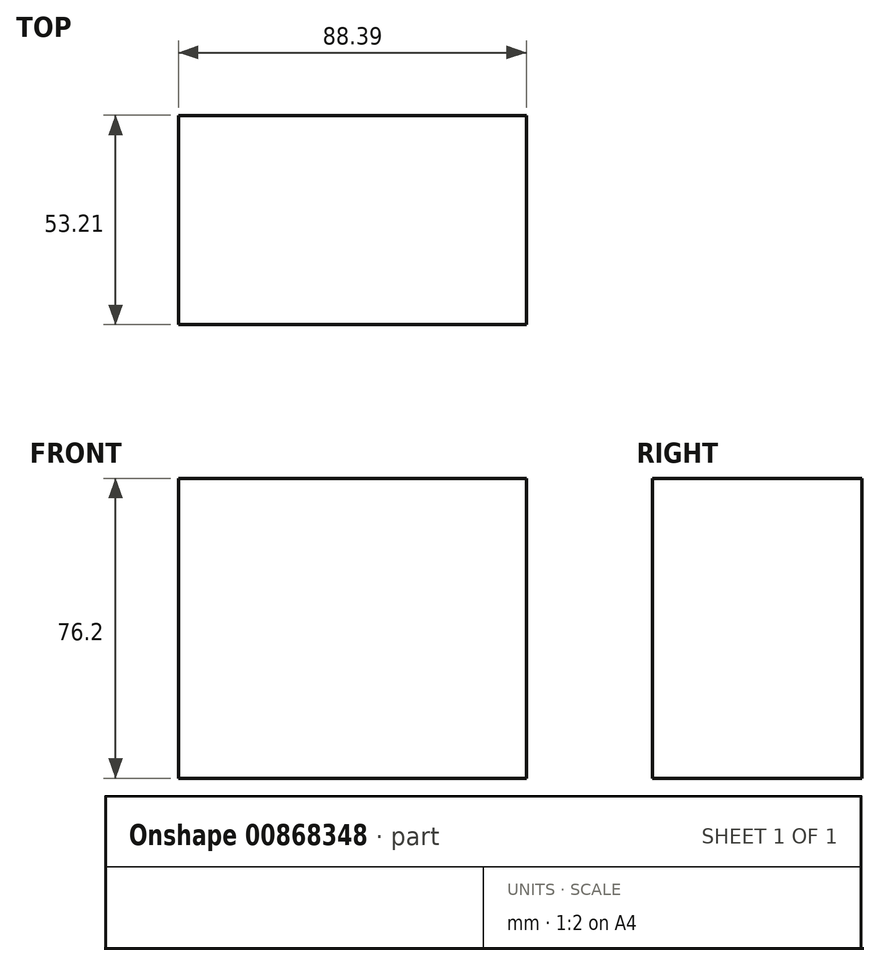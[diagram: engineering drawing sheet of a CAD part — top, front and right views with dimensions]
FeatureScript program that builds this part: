
annotation { "Feature Type Name" : "Feature", "Feature Type Description" : "" }
export const myFeature = defineFeature(function(context is Context, id is Id, definition is map)
    precondition{}
    {
        {
            var Q0;
            Q0=qCreatedBy(makeId("Top.planeOp"),FACE);
            var sketch = newSketch(context, id + "F0", { "sketchPlane" : qUnion([Q0])});
            skLineSegment(sketch, "E0.bottom", {"start": v(-27.25, 20.37) * mm, "end": v(61.14, 20.37) * mm});
            skLineSegment(sketch, "E0.top", {"start": v(-27.25, -32.84) * mm, "end": v(61.14, -32.84) * mm});
            skLineSegment(sketch, "E0.left", {"start": v(-27.25, 20.37) * mm, "end": v(-27.25, -32.84) * mm});
            skLineSegment(sketch, "E0.right", {"start": v(61.14, 20.37) * mm, "end": v(61.14, -32.84) * mm});
            skSolve(sketch);
        }
        {
            var Q0;
            Q0=makeQuery(id+"F0.imprint","IMPRINT",FACE,{"disambiguationData":[TD([[makeQuery(id+"F0.imprint","IMPRINT",EDGE,{"derivedFrom":sQuery(id+"F0.wireOp",EDGE,"E0.bottom")}),-1.0]])]});
            var sketch = newSketch(context, id + "F1", { "sketchPlane" : qUnion([Q0])});
            skSolve(sketch);
        }
        {
            var Q0;
            Q0=makeQuery(id+"F1.imprint","IMPRINT",FACE,{"disambiguationData":[TD([[makeQuery(id+"F1.imprint","IMPRINT",EDGE,{"derivedFrom":makeQuery(id+"F0.imprint","IMPRINT",EDGE,{"derivedFrom":sQuery(id+"F0.wireOp",EDGE,"E0.bottom")})}),-1.0]])]});
            extrude(context, id + "F2", {"entities" : qUnion([Q0]), "depth" : 76.2 * mm, "offsetDistance" : 25.4 * mm});
        }
    });
